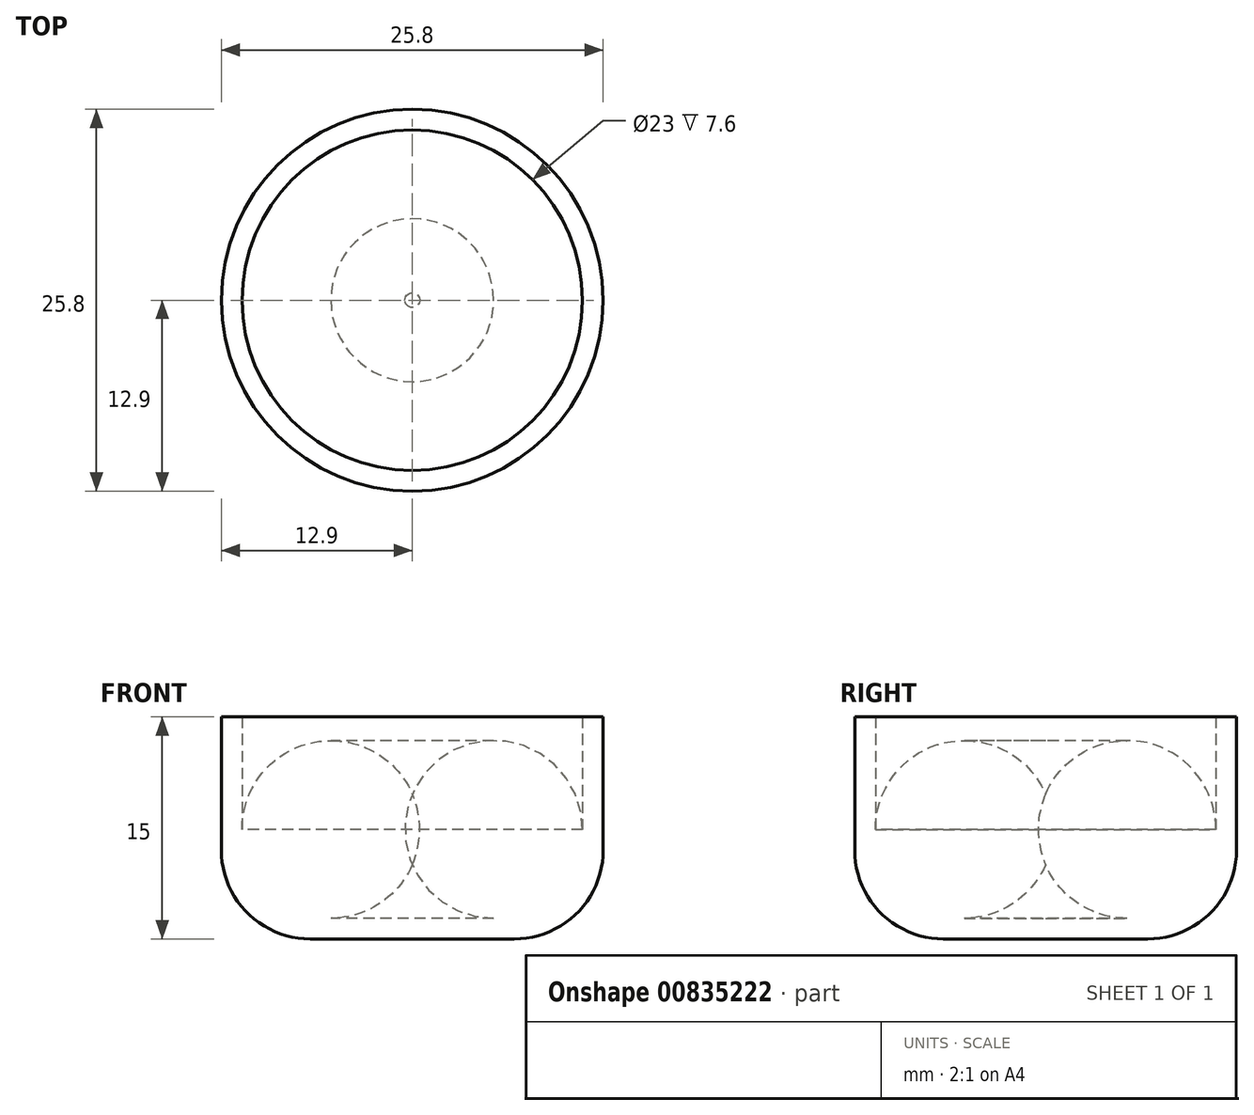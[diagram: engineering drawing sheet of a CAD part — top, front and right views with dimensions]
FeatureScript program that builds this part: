
annotation { "Feature Type Name" : "Feature", "Feature Type Description" : "" }
export const myFeature = defineFeature(function(context is Context, id is Id, definition is map)
    precondition{}
    {
        {
            var Q0;
            Q0=qCreatedBy(makeId("Top.planeOp"),FACE);
            var sketch = newSketch(context, id + "F0", { "sketchPlane" : qUnion([Q0])});
            skCircle(sketch, "E0", {"center": v(0, 0) * mm, "radius": 12.9 * mm});
            skSolve(sketch);
        }
        {
            var Q0;
            Q0=makeQuery(id+"F0.imprint","IMPRINT",FACE,{"disambiguationData":[TD([[makeQuery(id+"F0.imprint","IMPRINT",EDGE,{"derivedFrom":sQuery(id+"F0.wireOp",EDGE,"E0")}),1.0]])]});
            extrude(context, id + "F1", {"entities" : qUnion([Q0]), "depth" : 15 * mm, "offsetDistance" : 25.4 * mm});
        }
        {
            var Q0;
            Q0=makeQuery(id+"F1.opExtrude","CAP_FACE",FACE,{"disambiguationData":[OSD([sQuery(id+"F0.wireOp",EDGE,"E0")])],"isStart":false});
            shell(context, id + "F2", {"entities" : qUnion([Q0]), "thickness" : 1.4 * mm});
        }
        {
            var Q0;
            {var subQ0=sQuery(id+"F0.wireOp",EDGE,"E0");Q0=makeQuery(id+"F2.opShell","OFFSET_EDGE",EDGE,{"disambiguationData":[OSD([subQ0]),TDD([makeQuery(id+"F1.opExtrude","CAP_EDGE",EDGE,{"disambiguationData":[OSD([subQ0])],"isStart":true})])]});}
            var Q1;
            Q1=makeQuery(id+"F1.opExtrude","CAP_EDGE",EDGE,{"disambiguationData":[OSD([sQuery(id+"F0.wireOp",EDGE,"E0")])],"isStart":true});
            fillet(context, id + "F3", {"entities" : qUnion([Q0, Q1]), "radius" : 6 * mm, "tangentPropagation" : true, "allowEdgeOverflow" : false});
        }
    });
